# Revit family: PX_FD_HERBISH HOLES PC HB125HADJ
name_source: partatom
category: Plumbing Fixtures
revit_build: Autodesk Revit 2015 (Build: 20140223_1515(x64)
units: mm (PartAtom-declared; Revit-internal decimal feet)

## types (1)
- HERBISH HOLES PC HB125HADJ
    Description = HERBISH DRAIN WITH HOLES
    Manufacturer = Metal Spinning (Pty) Ltd
    Model = PC HB125HADJ
    Notes = The Herbish® HB 125 H is a unique Full Flow Floor Drain with the following features: 
	• Manufactured in Stainless Steel to ensure acid corrosion and stain resistance. 
	• A 70mm water seal to ensure an odour-free operation. 
	• Smooth surfaces for easy cleaning. 
	• Minimum dirt collection and high flow rates.
	• Easy to dismantle for cleaning, discharge pipe becomes fully accessible
    Stainless Steel = Stainless Steel
    Tolani civil Projects cc URL = www.tcpbim.co.za
    URL = http://www.metspin.co.za

## geometry (parser evidence)
native form markers: Sweep x2
no freeform markers — native parametric forms only
